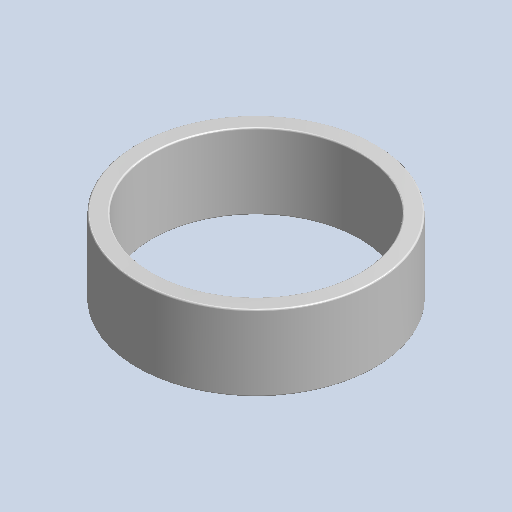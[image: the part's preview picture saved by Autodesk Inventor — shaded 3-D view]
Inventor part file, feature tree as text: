
AUTODESK INVENTOR PART (.ipt)
format: ipt  version: 2022 (Build 260153000, 153)  size: 103,424 bytes
history: mixed  units: mm (DEFAULTED — no unit token found)
features: other x8, fillet x1, imported_body x1
bodies: Body1 (imported_parasolid)
feature tree (10):
  other  "Sólido1"
  other  "Origen"
  other  "Plano YZ"
  other  "Plano XZ"
  other  "Plano XY"
  other  "Eje X"
  other  "Eje Y"
  other  "Eje Z"
  fillet  "Redondeo1"  [1 undecoded]
  imported_body  NMx_Import_Brep_tag  [imported B-rep: ~8 faces, bbox_mm=[0.0, 5.0, 1.05]]
note: 1 required parameter value undecoded (feature->parameter linkage not recoverable at this tier; creation-order binding heuristic only, values carry confidence <= 0.55)
